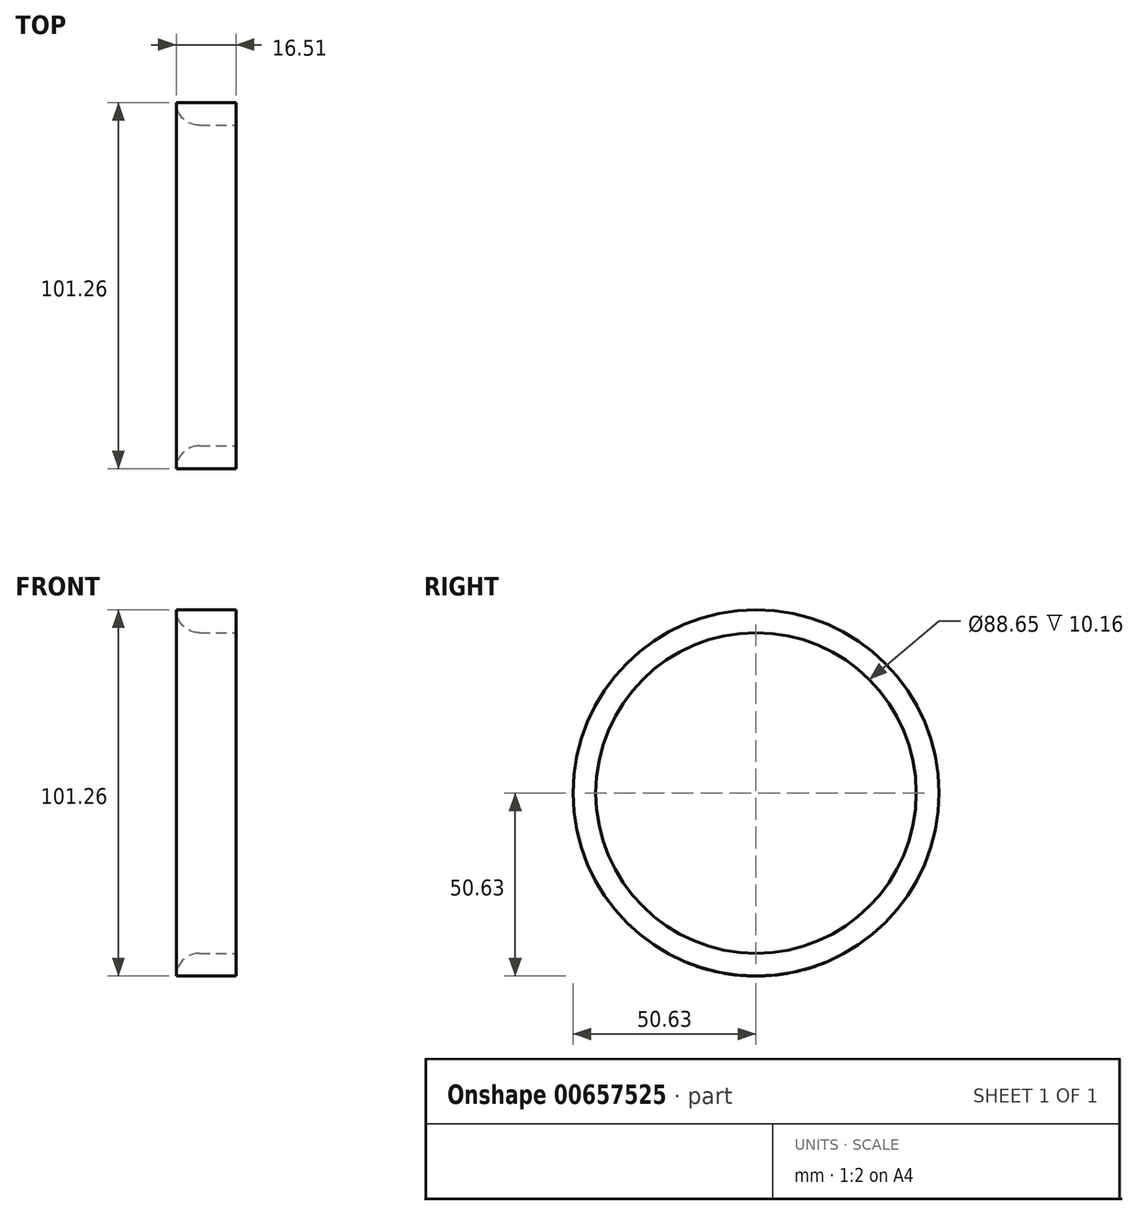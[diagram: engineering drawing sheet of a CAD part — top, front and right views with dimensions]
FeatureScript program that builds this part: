
annotation { "Feature Type Name" : "Feature", "Feature Type Description" : "" }
export const myFeature = defineFeature(function(context is Context, id is Id, definition is map)
    precondition{}
    {
        {
            var Q0;
            Q0=qCreatedBy(makeId("Front.planeOp"),FACE);
            var sketch = newSketch(context, id + "F0", { "sketchPlane" : qUnion([Q0])});
            skLineSegment(sketch, "E0", {"start": v(0, 0) * mm, "end": v(-80.85, 0) * mm});
            skLineSegment(sketch, "E1.bottom", {"start": v(0, 25.5) * mm, "end": v(-63.5, 25.5) * mm});
            skLineSegment(sketch, "E1.top", {"start": v(0, 50.63) * mm, "end": v(-63.5, 50.63) * mm});
            skLineSegment(sketch, "E1.left", {"start": v(0, 25.5) * mm, "end": v(0, 50.63) * mm});
            skLineSegment(sketch, "E1.right", {"start": v(-63.5, 25.5) * mm, "end": v(-63.5, 50.63) * mm});
            skLineSegment(sketch, "E2.bottom", {"start": v(-55.1, 50.63) * mm, "end": v(-52.32, 50.63) * mm});
            skLineSegment(sketch, "E2.right", {"start": v(-52.32, 51.85) * mm, "end": v(-52.32, 50.63) * mm});
            skLineSegment(sketch, "E3.bottom", {"start": v(-30.48, 50.63) * mm, "end": v(-22.7, 50.63) * mm});
            skLineSegment(sketch, "E3.top", {"start": v(-30.48, 46.11) * mm, "end": v(-22.7, 46.11) * mm});
            skLineSegment(sketch, "E3.left", {"start": v(-30.48, 50.63) * mm, "end": v(-30.48, 46.11) * mm});
            skLineSegment(sketch, "E3.right", {"start": v(-22.7, 50.63) * mm, "end": v(-22.7, 46.11) * mm});
            skLineSegment(sketch, "E4.bottom", {"start": v(0, 44.32) * mm, "end": v(-10.16, 44.32) * mm});
            skLineSegment(sketch, "E4.top", {"start": v(0, 50.63) * mm, "end": v(-16.51, 50.63) * mm});
            skLineSegment(sketch, "E4.left", {"start": v(0, 44.32) * mm, "end": v(0, 50.63) * mm});
            skLineSegment(sketch, "E4.right", {"start": v(-16.51, 50.63) * mm, "end": v(-16.51, 50.67) * mm});
            skLineSegment(sketch, "E5.bottom", {"start": v(-60.86, 25.5) * mm, "end": v(-57.84, 25.5) * mm});
            skLineSegment(sketch, "E5.top", {"start": v(-60.86, 29.85) * mm, "end": v(-57.84, 29.85) * mm});
            skLineSegment(sketch, "E5.left", {"start": v(-60.86, 25.5) * mm, "end": v(-60.86, 29.84) * mm});
            skLineSegment(sketch, "E5.right", {"start": v(-57.84, 25.5) * mm, "end": v(-57.84, 29.85) * mm});
            skLineSegment(sketch, "E6.bottom", {"start": v(-51.38, 25.5) * mm, "end": v(-41.02, 25.5) * mm});
            skLineSegment(sketch, "E6.top", {"start": v(-51.38, 32.58) * mm, "end": v(-41.02, 32.58) * mm});
            skLineSegment(sketch, "E6.left", {"start": v(-51.38, 25.5) * mm, "end": v(-51.38, 32.58) * mm});
            skLineSegment(sketch, "E6.right", {"start": v(-41.02, 25.5) * mm, "end": v(-41.02, 32.58) * mm});
            skPoint(sketch, "E7.visualSharp", {"position": v(-16.51, 44.32) * mm});
            skArc(sketch, "E7.filletArc", {"start": v(-16.51, 50.67) * mm, "mid": v(-14.65, 46.18) * mm, "end": v(-10.16, 44.32) * mm});
            skLineSegment(sketch, "E8", {"start": v(-56.13, 48.04) * mm, "end": v(-63.5, 48.04) * mm});
            skPoint(sketch, "E9.visualSharp", {"position": v(-52.32, 48.04) * mm});
            skArc(sketch, "E9.filletArc", {"start": v(-56.13, 48.04) * mm, "mid": v(-53.44, 49.16) * mm, "end": v(-52.32, 51.85) * mm});
            skPoint(sketch, "E10", {"position": v(-52.52, 50.63) * mm});
            skSolve(sketch);
        }
        {
            var Q0;
            {var subQ2=sQuery(id+"F0.wireOp",EDGE,"E1.left");Q0=makeQuery(id+"F0.imprint","IMPRINT",FACE,{"disambiguationData":[TD([[makeQuery(id+"F0.imprint","IMPRINT",EDGE,{"derivedFrom":subQ2}),1.0]])]});}
            var Q1;
            Q1=sQuery(id+"F0.wireOp",EDGE,"E0");
            revolve(context, id + "F1", {"entities" : qUnion([Q0]), "axis" : qUnion([Q1]), "revolveType" : RevolveType.FULL});
        }
    });
